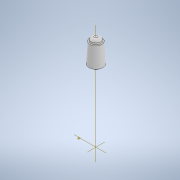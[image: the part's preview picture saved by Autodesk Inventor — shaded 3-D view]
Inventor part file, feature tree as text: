
AUTODESK INVENTOR PART (.ipt)
format: ipt  version: 2021 (Build 250183000, 183)  size: 1,273,856 bytes
history: native  units: mm
features: sketch x31, extrude x29, fillet x16, other x6, plane x5, sweep x3
ambient origin geometry x8: Origin, YZ Plane, XZ Plane, XY Plane, X Axis, Y Axis, Z Axis, Center Point
bodies: Body1 (feature_tree), Body2 (feature_tree), Body3 (feature_tree), Body4 (feature_tree)
feature tree (90):
  other  "Soyuz Core Stage"
  extrude  "Core Airframe"  Depth=133.0mm TaperAngle=0.0deg
  extrude  "Vernier Housing"  Depth=3.4mm
  extrude  "Main Engine Extrude"  TaperAngle=0.0deg  [1 undecoded]
  extrude  "Main Engine Cut"  Depth=3.4mm
  extrude  "Vernier Nozzels"  Depth=3.4mm
  extrude  "Extrusion11"  Depth=3.4mm
  extrude  "Extrusion12"  Depth=5.5mm
  sweep  "Sweep1"
  sweep  "Booster Nosecone"
  extrude  "Extrusion16"  Depth=4.5mm
  plane  "Work Plane6"
  extrude  "Extrusion17"  Depth=4.5mm
  plane  "Work Plane5"
  extrude  "Extrusion18"  Depth=4.5mm
  fillet  "Fillet11"  Radius=4.5mm
  fillet  "Fillet12"  Radius=6.0mm
  fillet  "Fillet13"  Radius=2.0mm
  fillet  "Fillet14"  Radius=10.5mm
  extrude  "Booster Lock Extrusion"  Depth=2.0mm
  extrude  "Booster Lock Cut"  Depth=10.5mm
  other  "Work Point1"
  plane  "Work Plane1"
  sweep  "Sweep4"
  extrude  "Extrusion26"  TaperAngle=0.0deg  [1 undecoded]
  fillet  "Fillet16"  [1 undecoded]
  plane  "Work Plane4"
  other  "Work Point2"
  plane  "Work Plane2"
  extrude  "Extrusion27"  Depth=5.0mm
  extrude  "Extrusion28"  Depth=5.0mm
  extrude  "Extrusion29"  Depth=5.0mm
  fillet  "Fillet17"  [1 undecoded]
  fillet  "Fillet18"  [1 undecoded]
  fillet  "Fillet19"  [1 undecoded]
  extrude  "Extrusion30"  Depth=9.0mm
  fillet  "Fillet20"  Radius=28.0mm
  fillet  "Fillet21"  Radius=25.0mm
  fillet  "Fillet22"  [1 undecoded]
  extrude  "Extrusion31"  Depth=13.0mm
  extrude  "Extrusion32"  TaperAngle=0.0deg  [1 undecoded]
  extrude  "Extrusion33"  TaperAngle=0.0deg  [1 undecoded]
  extrude  "Extrusion34"  TaperAngle=0.0deg  [1 undecoded]
  fillet  "Fillet23"  [1 undecoded]
  fillet  "Fillet24"  Radius=17.0mm
  fillet  "Fillet25"  Radius=23.0mm
  fillet  "Fillet26"  [1 undecoded]
  extrude  "Extrusion35"  TaperAngle=0.0deg  [1 undecoded]
  extrude  "Extrusion36"  Depth=15.0mm
  extrude  "Extrusion50"  Depth=1.5mm
  fillet  "Fillet75"  [1 undecoded]
  extrude  "Extrusion51"  Depth=3.0mm TaperAngle=0.0deg
  extrude  "Extrusion52"  Depth=0.5mm TaperAngle=0.0deg
  sketch  "Sketch5"  dims[d0=20.0mm d1=133.0mm d2=0.0mm]
  sketch  "Sketch6"  dims[d7=0.0mm d9=3.4mm]
  sketch  "Sketch15"  dims[d10=3.4mm d12=0.0mm]
  sketch  "Sketch16"  dims[d15=3.4mm d18=3.4mm]
  sketch  "Sketch20"  dims[d20=3.4mm d21=3.4mm]
  other  "Soyuz Booster"
  sketch  "Sketch27"  dims[d25=3.4mm d26=3.4mm]
  sketch  "Sketch28"  dims[d33=7.0mm d34=0.0mm d47=5.5mm]
  sketch  "Sketch29"  dims[d48=5.5mm d49=5.5mm]
  sketch  "Sketch31"  dims[d50=5.5mm d52=4.5mm]
  sketch  "Sketch32"  dims[d53=4.5mm d54=4.5mm]
  sketch  "Sketch34"  dims[d55=4.5mm d56=4.5mm]
  sketch  "Sketch35"  dims[d57=4.5mm d58=4.5mm d59=4.5mm d60=6.0mm d61=2.094395mm d62=2.0mm d63=10.5mm]
  sketch  "Sketch41"  dims[d70=0.0mm d71=0.0mm d72=0.0mm]
  sketch  "Sketch42"  dims[d73=0.0mm d74=5.0mm d75=1.396263mm]
  sketch  "Sketch43"  dims[d76=5.0mm d77=5.0mm]
  sketch  "Sketch45"  dims[d78=5.0mm d79=5.0mm d80=0.0mm d81=0.0mm d82=0.0mm]
  sketch  "Sketch49"  dims[d83=0.0mm d85=9.0mm d86=-1.396263mm d156=28.0mm d160=25.0mm d161=0.0mm]
  sketch  "Sketch50"  dims[d166=13.0mm d167=13.0mm d168=13.0mm d171=13.0mm]
  sketch  "Sketch51"  dims[d174=27.0mm d175=0.0mm d177=0.0mm]
  sketch  "Sketch52"  dims[d178=0.0mm d179=0.0mm]
  sketch  "Sketch53"  dims[d180=38.0mm d181=1.658063mm d236=0.0mm d237=0.0mm d278=17.0mm d280=23.0mm d281=-0.610865mm d282=0.0mm]
  sketch  "Sketch54"  dims[d304=0.0mm d309=0.0mm]
  sketch  "Sketch55"  dims[d311=15.0mm d312=15.0mm]
  sketch  "Sketch56"  dims[d313=19.0mm d314=1.5mm d316=-2.356194mm d317=0.0mm]
  other  "Core Stage Part 2"
  sketch  "Sketch57"  dims[d318=0.0mm d330=3.0mm d331=0.0mm]
  sketch  "Sketch81"  dims[d334=0.5mm d335=0.0mm d338=0.5mm d339=0.0mm]
  sketch  "Sketch82"  dims[d342=3.0mm d343=3.0mm]
  sketch  "Sketch83"  dims[d344=3.0mm d345=6.0mm d346=1.2mm d347=1.2mm d348=1.2mm d349=1.2mm d350=0.0mm d351=0.0mm d352=0.0mm d353=0.0mm d354=14.5mm d355=14.5mm d356=14.5mm d357=14.5mm d358=11.5mm d359=1.745329mm d361=2.2mm d362=1.6mm d363=0.0mm d364=4.1mm d365=-1.745329mm d366=0.0mm d367=1.6mm d368=2.2mm d369=0.0mm d370=1.6mm d371=2.2mm d372=1.6mm d373=0.0mm d374=2.2mm d397=5.5mm d398=4.5mm d400=5.5mm d401=4.5mm d402=4.5mm d403=5.5mm d404=4.5mm d406=5.5mm d410=2.094395mm d411=6.0mm d412=5.0mm d413=0.0mm d414=5.0mm d415=0.0mm d416=0.0mm d417=5.0mm d418=0.0mm d419=5.0mm d421=-1.396263mm d422=9.0mm d423=0.0mm d424=0.0mm d425=0.0mm d426=0.0mm d427=9.0mm d428=9.0mm d429=9.0mm d430=9.0mm d431=6.0mm d432=0.0mm d446=1.396263mm d447=5.0mm d449=2.0mm d450=2.0mm d452=21.5mm d453=21.5mm d454=6.2mm d455=6.2mm d456=0.5mm d459=0.5mm d460=0.5mm d461=0.0mm d464=0.5mm d465=1.3mm d466=0.0mm d467=1.3mm d468=3.0mm d470=3.0mm d472=0.0mm d473=0.0mm d475=6.0mm d476=1.0mm d477=6.0mm d478=0.0mm d479=-0.202458mm d480=0.0mm d481=5.0mm d482=2.0mm d483=2.0mm d484=0.0mm d485=10.0mm d486=0.0mm d487=0.5mm d489=3.0mm d490=1.0mm d491=1.0mm d492=28.0mm d493=0.5mm d494=0.0mm d518=0.0mm d521=0.0mm d522=0.0mm d524=0.0mm d525=0.5mm d526=0.0mm d527=3.0mm d528=3.0mm d529=0.1mm d530=20.0mm d531=7.0mm d532=0.0mm d538=0.0mm d539=0.0mm d540=0.0mm d541=0.0mm d542=0.0mm d543=0.0mm d544=0.0mm d545=0.0mm d546=0.0mm d547=0.0mm d548=0.0mm d549=0.0mm d550=12.5mm d551=12.5mm d553=12.5mm d554=12.5mm d556=0.0mm d557=0.0mm d561=0.0mm d562=0.0mm d563=0.0mm d564=0.0mm d566=0.0mm d567=0.0mm d568=0.0mm d571=0.0mm d572=0.0mm d573=0.0mm d575=6.0mm d576=6.0mm d577=6.0mm d578=6.0mm d579=0.0mm d581=0.0mm d582=5.0mm d583=-6.108652mm d584=1.0mm d585=1.0mm d593=2.0mm d594=3.0mm d604=1.0mm d608=0.0mm d609=2.0mm d610=0.0mm d611=3.0mm d612=1.0mm d614=0.0mm d617=1.0mm d618=0.781667mm d619=2.5mm d649=12.5mm d650=12.5mm d651=0.5mm d652=0.0mm d653=0.5mm d654=4.5mm d655=4.5mm d657=0.0mm d658=1.0mm d659=1.377412mm d660=1.377mm d661=4.5mm d662=1.0mm d663=0.5mm d664=0.0mm d665=4.5mm d666=1.377mm d667=1.0mm d668=4.5mm d669=1.377mm d670=1.0mm d671=0.5mm d672=0.0mm d673=4.5mm d674=1.377mm d675=4.5mm d676=1.377mm d677=1.0mm d678=1.0mm d679=0.5mm d680=0.0mm d681=4.5mm d682=4.5mm d683=1.377mm d684=1.377mm d685=1.0mm d686=1.0mm d687=0.5mm d688=0.0mm d689=0.5mm d690=0.2mm d691=0.3mm d692=1.0mm d694=0.0mm d695=0.0mm d696=0.1mm d697=5.0mm d698=0.0mm d699=0.0mm d700=0.0mm d702=50.0mm d703=-0.541052mm d709=0.0mm d993=0.0mm d994=0.0mm d995=2.5mm d996=5.0mm d997=0.0mm d998=8.0mm d999=0.0mm d1000=0.0mm d1001=0.0mm d1002=0.0mm d1003=0.0mm d1004=0.0mm d1005=4.0mm d1006=0.0mm d1007=0.0mm d1008=0.0mm d1009=0.0mm d1010=0.0mm d1011=0.0mm d1012=0.0mm d1013=4.0mm d1014=0.0mm d194=0.5mm d195=0.872665mm d196=0.5mm d197=0.872665mm d261=0.5mm d262=0.872665mm d263=0.5mm d264=0.872665mm d808=0.5mm d809=0.872665mm d810=0.5mm d811=0.872665mm]
  other  "Interstage 1"
  extrude  "Extrusion23"  Depth=3.0mm
  extrude  "Extrusion24"  Depth=0.5mm
  extrude  "Extrusion25"  Depth=0.5mm
  sketch  "Sketch38"  dims[d64=2.0mm d65=2.0mm]
  sketch  "Sketch39"  dims[d66=2.0mm d67=10.5mm]
  sketch  "Sketch40"  dims[d68=10.5mm d69=10.5mm]
note: 14 required parameter values undecoded (feature->parameter linkage not recoverable at this tier; creation-order binding heuristic only, values carry confidence <= 0.55)
